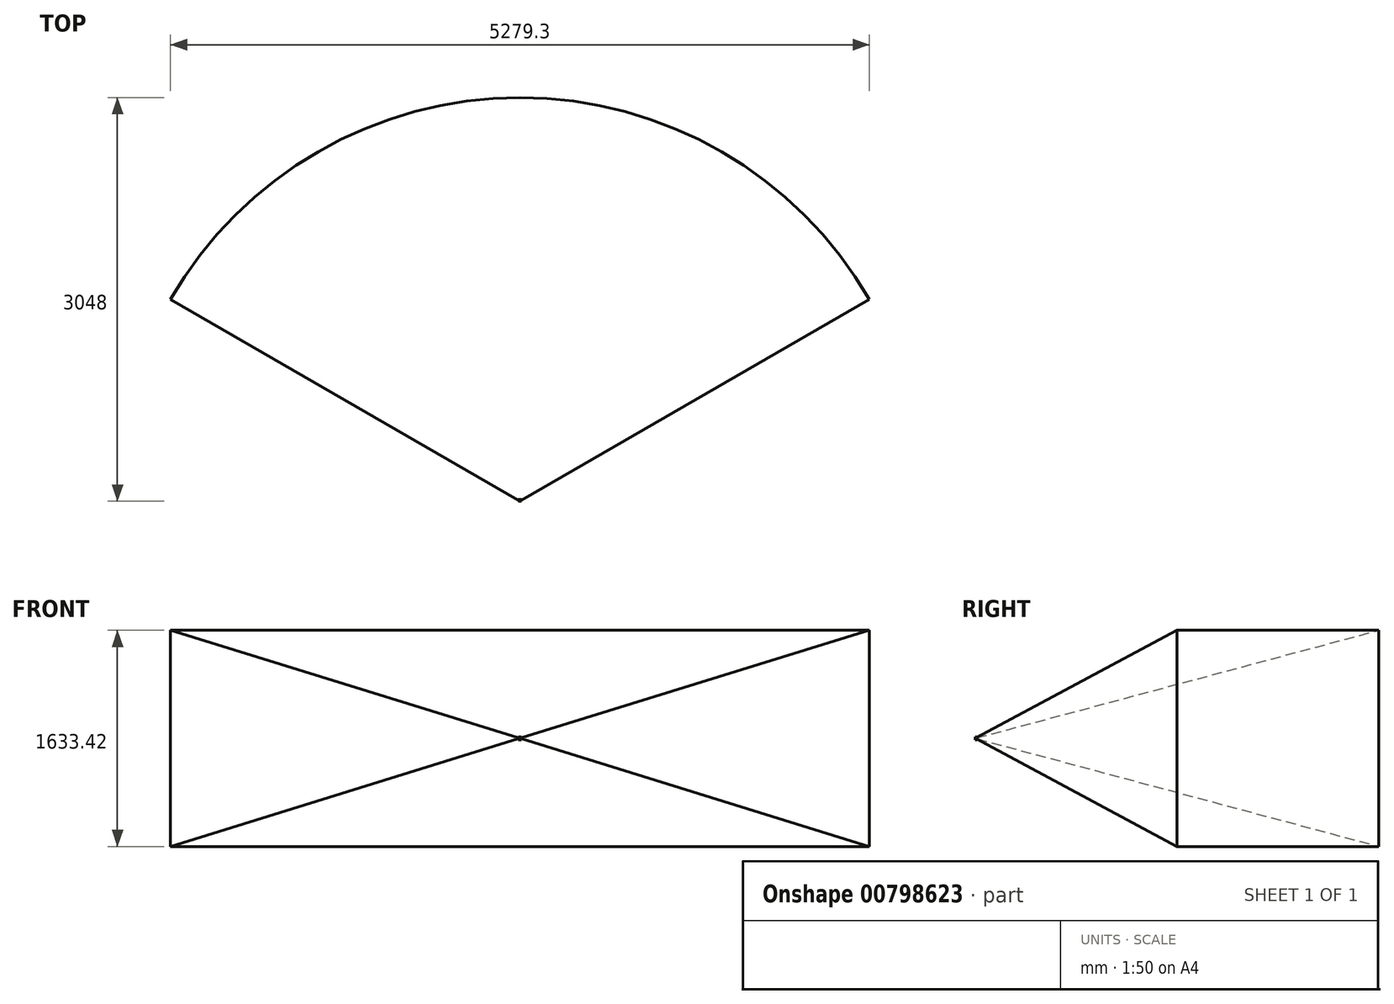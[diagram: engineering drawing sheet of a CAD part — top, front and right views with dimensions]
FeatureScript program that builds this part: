
annotation { "Feature Type Name" : "Feature", "Feature Type Description" : "" }
export const myFeature = defineFeature(function(context is Context, id is Id, definition is map)
    precondition{}
    {
        {
            var Q0;
            Q0=qCreatedBy(makeId("Right.planeOp"),FACE);
            var sketch = newSketch(context, id + "F0", { "sketchPlane" : qUnion([Q0])});
            skLineSegment(sketch, "E0", {"start": v(0, 0) * mm, "end": v(3048, 816.7) * mm});
            skLineSegment(sketch, "E1", {"start": v(3048, 816.7) * mm, "end": v(3048, -816.7) * mm});
            skLineSegment(sketch, "E2", {"start": v(3048, -816.7) * mm, "end": v(0, 0) * mm});
            skLineSegment(sketch, "E3", {"start": v(0, 0) * mm, "end": v(3048, 0) * mm});
            skLineSegment(sketch, "E4", {"start": v(0, 22.16) * mm, "end": v(0, -19.91) * mm});
            skSolve(sketch);
        }
        {
            var Q0;
            Q0 = qSketchRegion(id + "F0", true);
            var Q1;
            Q1=sQuery(id+"F0.wireOp",EDGE,"E4");
            revolve(context, id + "F1", {"surfaceOperationType" : NewSurfaceOperationType.NEW, "entities" : qUnion([Q0]), "axis" : qUnion([Q1]), "revolveType" : RevolveType.SYMMETRIC, "angle" : 120 * degree});
        }
        {
            var Q0;
            Q0=qCreatedBy(makeId("Front.planeOp"),FACE);
            var sketch = newSketch(context, id + "F2", { "sketchPlane" : qUnion([Q0])});
            skLineSegment(sketch, "E5.bottom", {"start": v(10.34, -10.5) * mm, "end": v(-10.34, -10.5) * mm});
            skLineSegment(sketch, "E5.top", {"start": v(10.34, 10.5) * mm, "end": v(-10.34, 10.5) * mm});
            skLineSegment(sketch, "E5.left", {"start": v(10.34, -10.5) * mm, "end": v(10.34, 10.5) * mm});
            skLineSegment(sketch, "E5.right", {"start": v(-10.34, -10.5) * mm, "end": v(-10.34, 10.5) * mm});
            skPoint(sketch, "E5.middle", {"position": v(0, 0) * mm});
            skSolve(sketch);
        }
        {
            var Q0;
            Q0 = qSketchRegion(id + "F2", true);
            extrude(context, id + "F3", {"entities" : qUnion([Q0]), "operationType" : NewBodyOperationType.ADD, "oppositeDirection" : true, "depth" : 12.7 * mm, "offsetDistance" : 25.4 * mm});
        }
    });
